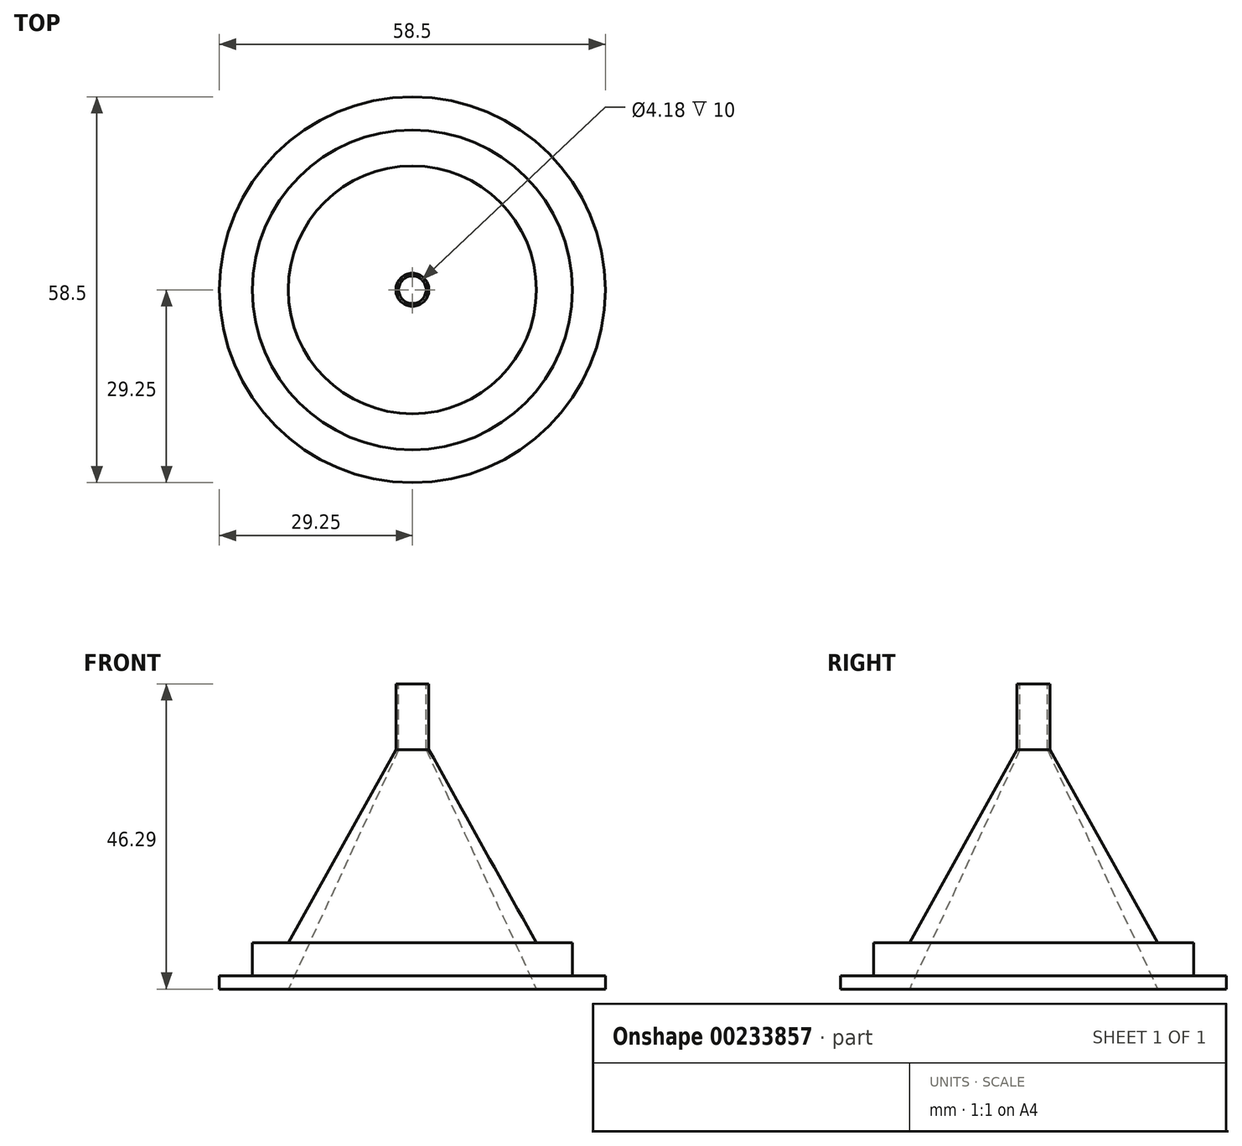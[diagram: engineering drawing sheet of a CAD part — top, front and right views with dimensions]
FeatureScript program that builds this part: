
annotation { "Feature Type Name" : "Feature", "Feature Type Description" : "" }
export const myFeature = defineFeature(function(context is Context, id is Id, definition is map)
    precondition{}
    {
        {
            var Q0;
            Q0=qCreatedBy(makeId("Front.planeOp"),FACE);
            var sketch = newSketch(context, id + "F0", { "sketchPlane" : qUnion([Q0])});
            skLineSegment(sketch, "E0", {"start": v(0, 74.56) * mm, "end": v(0, -84.84) * mm, "construction": true});
            skLineSegment(sketch, "E1", {"start": v(29.25, 12.36) * mm, "end": v(29.25, -14.86) * mm, "construction": true});
            skLineSegment(sketch, "E2", {"start": v(2.5, 55.2) * mm, "end": v(2.5, 36.3) * mm, "construction": true});
            skLineSegment(sketch, "E3", {"start": v(29.25, 0) * mm, "end": v(18.8, 0) * mm});
            skLineSegment(sketch, "E4", {"start": v(29.25, 0) * mm, "end": v(29.25, 2) * mm});
            skLineSegment(sketch, "E5", {"start": v(2.5, 36.3) * mm, "end": v(2.5, 46.3) * mm});
            skPoint(sketch, "E5.endSnap0", {"position": v(2.5, 45.75) * mm});
            skLineSegment(sketch, "E6", {"start": v(2.5, 46.3) * mm, "end": v(2.1, 46.3) * mm});
            skLineSegment(sketch, "E7", {"start": v(2.1, 46.3) * mm, "end": v(2.1, 36.3) * mm});
            skLineSegment(sketch, "E8", {"start": v(29.25, 2) * mm, "end": v(24.25, 2) * mm});
            skLineSegment(sketch, "E9", {"start": v(18.8, -10.15) * mm, "end": v(18.8, 27.75) * mm, "construction": true});
            skLineSegment(sketch, "E10", {"start": v(24.25, 2) * mm, "end": v(24.25, 7) * mm});
            skLineSegment(sketch, "E11", {"start": v(18.8, 0) * mm, "end": v(2.09, 36.3) * mm});
            skLineSegment(sketch, "E12", {"start": v(24.25, 7) * mm, "end": v(18.8, 7) * mm});
            skLineSegment(sketch, "E13", {"start": v(18.8, 7) * mm, "end": v(2.5, 36.3) * mm});
            skSolve(sketch);
        }
        {
            var Q0;
            Q0=makeQuery(id+"F0.imprint","IMPRINT",FACE,{"disambiguationData":[TD([[makeQuery(id+"F0.imprint","IMPRINT",EDGE,{"derivedFrom":sQuery(id+"F0.wireOp",EDGE,"E3")}),-1.0]])]});
            var Q1;
            Q1=sQuery(id+"F0.wireOp",EDGE,"E0");
            revolve(context, id + "F1", {"entities" : qUnion([Q0]), "axis" : qUnion([Q1]), "revolveType" : RevolveType.FULL});
        }
    });
